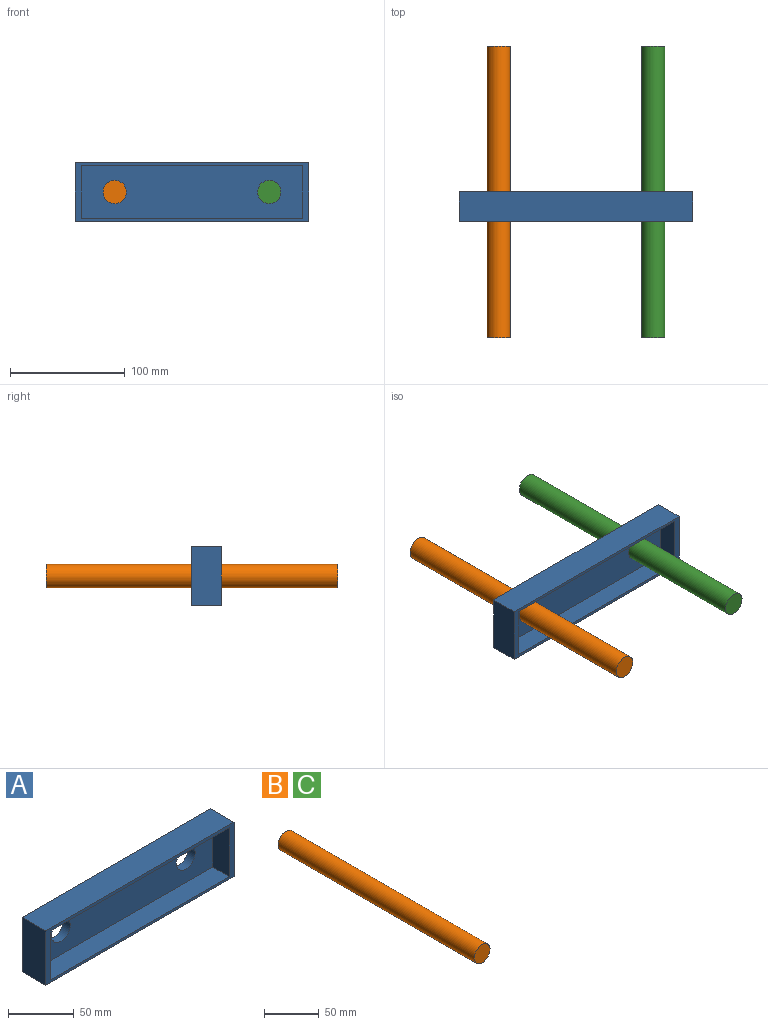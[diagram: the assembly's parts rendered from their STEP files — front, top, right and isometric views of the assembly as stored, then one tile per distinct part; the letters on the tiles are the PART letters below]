
ASSEMBLY  parts=3 mates=2
PART A: 13 faces, bbox 203.2x25.4x50.8 mm
  f0: cylinder r=10.16mm len=20.32mm, axis (0,1,0), area 486.4mm2, adj f7,f12
  f1: cylinder r=10.16mm len=20.32mm, axis (0,1,0), area 486.4mm2, adj f7,f12
  f2: plane 203.2x50.8mm, normal (0,-1,0), area 1496.8mm2, adj f3,f4,f5,f6,f8,f9,f10,f11
  f3: plane 203.2x25.4mm, normal (0,0,-1), area 5161.3mm2, adj f2,f4,f6,f7
  f4: plane 50.8x25.4mm, normal (1,0,0), area 1290.3mm2, adj f2,f3,f5,f7
  f5: plane 203.2x25.4mm, normal (0,0,1), area 5161.3mm2, adj f2,f4,f6,f7
  f6: plane 50.8x25.4mm, normal (-1,0,0), area 1290.3mm2, adj f2,f3,f5,f7
  f7: plane 203.2x50.8mm, normal (0,1,0), area 9674mm2, adj f0,f1,f3,f4,f5,f6
  f8: plane 193.04x17.78mm, normal (0,0,1), area 3432.3mm2, adj f2,f9,f11,f12
  f9: plane 45.72x17.78mm, normal (-1,0,0), area 812.9mm2, adj f2,f8,f10,f12
  f10: plane 193.04x17.78mm, normal (0,0,-1), area 3432.3mm2, adj f2,f9,f11,f12
  f11: plane 45.72x17.78mm, normal (1,0,0), area 812.9mm2, adj f2,f8,f10,f12
  f12: plane 193.04x45.72mm, normal (0,-1,0), area 8177.2mm2, adj f0,f1,f8,f9,f10,f11
PART B: 3 faces, bbox 20.3x254x20.3 mm
  f0: cylinder r=10.16mm len=254mm, axis (0,1,0), area 16214.6mm2, adj f1,f2
  f1: plane 20.32x20.32mm, normal (0,-1,0), area 324.3mm2, adj f0
  f2: plane 20.32x20.32mm, normal (0,1,0), area 324.3mm2, adj f0
PART C: same geometry as B
PLACE A t=(40.86,246,-119.97)mm
PLACE B t=(-26.45,246,-119.97)mm
PLACE C t=(108.17,246,-119.97)mm
MATE revolute B.f0 <-> A.f0  axis (0,1,0) through (-26.45,246,-119.97)mm
MATE revolute C.f0 <-> A.f1  axis (0,1,0) through (108.17,246,-119.97)mm
